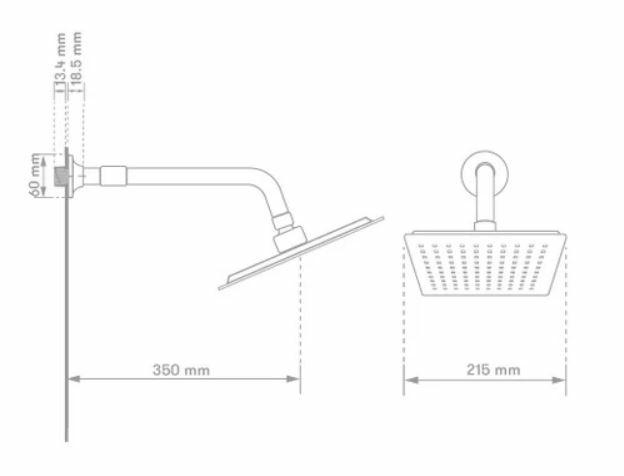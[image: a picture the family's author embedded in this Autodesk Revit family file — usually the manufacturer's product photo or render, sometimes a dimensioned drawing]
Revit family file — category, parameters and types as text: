
# Revit family: 01-3535-211-MEZCLADOR DUCHA SIN SALIDA TINA FIRENZE CRUZ
name_source: partatom
category: Plumbing Fixtures
revit_build: Autodesk Revit 2018 (Build: 20170223_1515(x64)
units: mm (PartAtom-declared; Revit-internal decimal feet)

## family parameters
Cut with Voids When Loaded = No
Host = Face
OmniClass Number = 23.31.11.00
Part Type = Normal
Room Calculation Point = No
Round Connector Dimension = Use Diameter
Shared = No

## types (1)
- 01-3535-211
    Alto = 60 mm  [stored 0.19685 ft]
    Ancho = 70 mm
    CW Connection = Yes
    Default Elevation = 0 mm  [stored 0 ft]
    Description = Mezclador ducha
    Distancia entre griferias = 203 mm
    Ficha tecnica = http://infotecnica.gricol.com
    Finish = Cromo Gricol
    HW Connection = Yes
    Manufacturer = Gricol
    Model = 01-3535-211
    Product Name = MEZCLADOR DUCHA SIN SALIDA TINA FIRENZE CRUZ
    Profundidad = 85 mm
    Sepacion entre registro y ducha = 790 mm
    Type Image = FIRENZE CUZ FOTO.jpg
    URL = https://www.gricol.com
    Vent Connection = No
    Waste Connection = No

note: [stored X ft] marks values corroborated as IEEE doubles in the binary element streams (Revit-internal decimal feet)

## geometry (parser evidence)
native form markers: Blend x4, Sweep x6
no freeform markers — native parametric forms only
